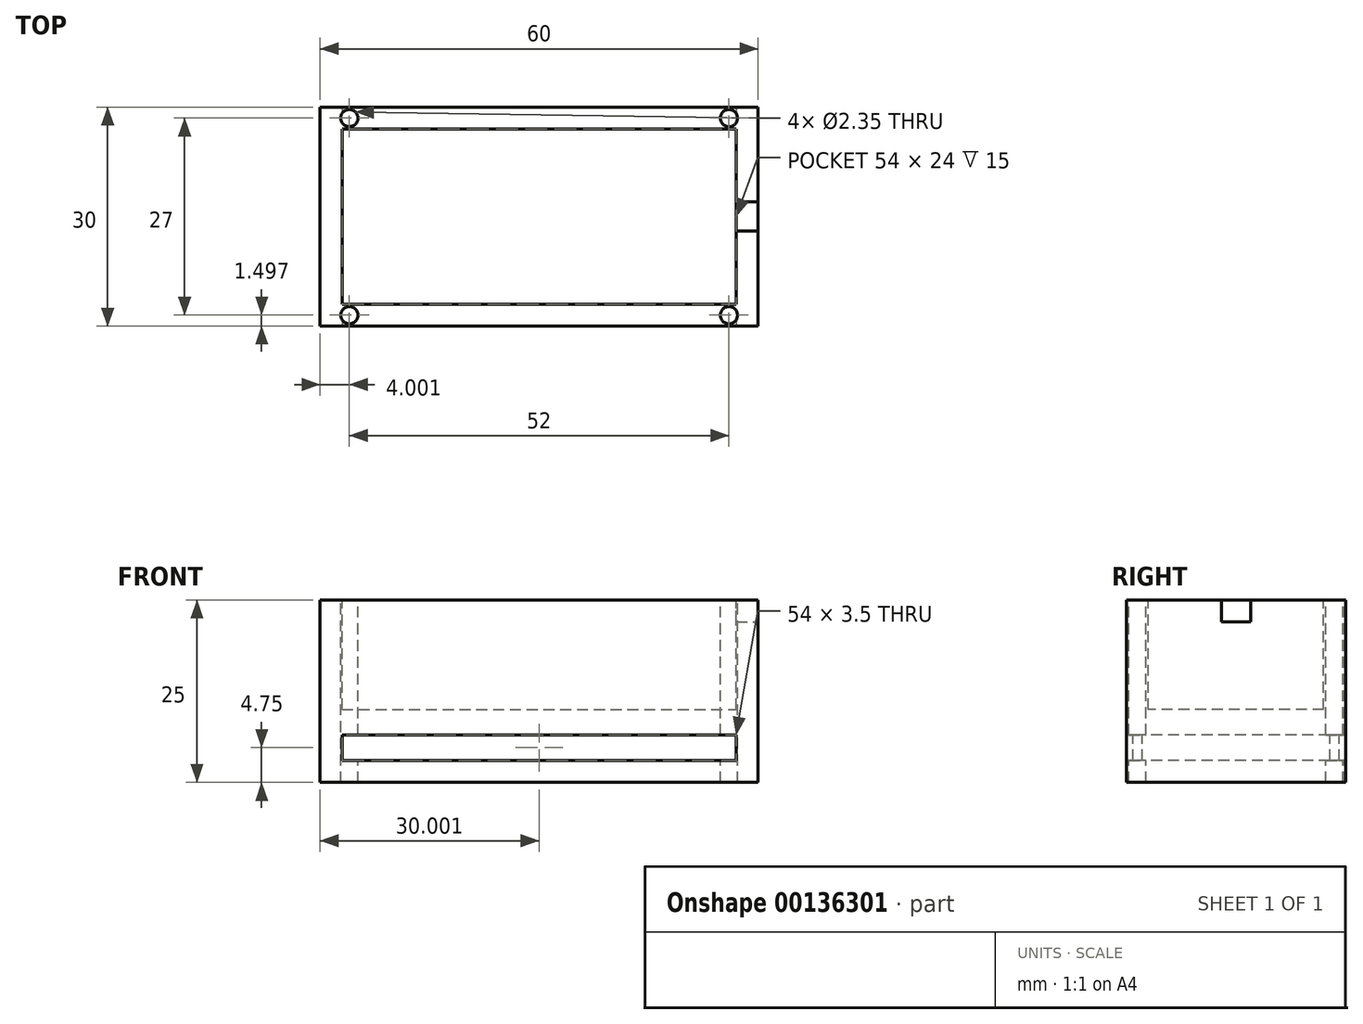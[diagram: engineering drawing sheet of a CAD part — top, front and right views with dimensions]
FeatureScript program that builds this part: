
annotation { "Feature Type Name" : "Feature", "Feature Type Description" : "" }
export const myFeature = defineFeature(function(context is Context, id is Id, definition is map)
    precondition{}
    {
        {
            var Q0;
            Q0=qCreatedBy(makeId("Top.planeOp"),FACE);
            var sketch = newSketch(context, id + "F0", { "sketchPlane" : qUnion([Q0])});
            skLineSegment(sketch, "E0.bottom", {"start": v(-30, 14.8) * mm, "end": v(30, 14.8) * mm});
            skLineSegment(sketch, "E0.top", {"start": v(-30, -15.2) * mm, "end": v(30, -15.2) * mm});
            skLineSegment(sketch, "E0.left", {"start": v(-30, 14.8) * mm, "end": v(-30, -15.2) * mm});
            skLineSegment(sketch, "E0.right", {"start": v(30, 14.8) * mm, "end": v(30, -15.2) * mm});
            skSolve(sketch);
        }
        {
            var Q0;
            Q0 = qSketchRegion(id + "F0", true);
            extrude(context, id + "F1", {"entities" : qUnion([Q0]), "depth" : 25 * mm});
        }
        {
            var Q0;
            Q0=makeQuery(id+"F1.opExtrude","SWEPT_FACE",FACE,{"disambiguationData":[OSD([sQuery(id+"F0.wireOp",EDGE,"E0.top")])]});
            var sketch = newSketch(context, id + "F2", { "sketchPlane" : qUnion([Q0])});
            skLineSegment(sketch, "E1.bottom", {"start": v(-27, 6.5) * mm, "end": v(27, 6.5) * mm});
            skLineSegment(sketch, "E1.top", {"start": v(-27, 3) * mm, "end": v(27, 3) * mm});
            skLineSegment(sketch, "E1.left", {"start": v(-27, 6.5) * mm, "end": v(-27, 3) * mm});
            skLineSegment(sketch, "E1.right", {"start": v(27, 6.5) * mm, "end": v(27, 3) * mm});
            skSolve(sketch);
        }
        {
            var Q0;
            Q0 = qSketchRegion(id + "F2", true);
            extrude(context, id + "F3", {"entities" : qUnion([Q0]), "operationType" : NewBodyOperationType.REMOVE, "endBound" : BoundingType.THROUGH_ALL, "oppositeDirection" : true, "depth" : 25 * mm});
        }
        {
            var Q0;
            Q0=makeQuery(id+"F1.opExtrude","CAP_FACE",FACE,{"disambiguationData":[OSD([sQuery(id+"F0.wireOp",EDGE,"E0.bottom"),sQuery(id+"F0.wireOp",EDGE,"E0.top"),sQuery(id+"F0.wireOp",EDGE,"E0.left"),sQuery(id+"F0.wireOp",EDGE,"E0.right")])],"isStart":false});
            var sketch = newSketch(context, id + "F4", { "sketchPlane" : qUnion([Q0])});
            skLineSegment(sketch, "E2.bottom", {"start": v(-27, 11.8) * mm, "end": v(27, 11.8) * mm});
            skLineSegment(sketch, "E2.top", {"start": v(-27, -12.2) * mm, "end": v(27, -12.2) * mm});
            skLineSegment(sketch, "E2.left", {"start": v(-27, 11.8) * mm, "end": v(-27, -12.2) * mm});
            skLineSegment(sketch, "E2.right", {"start": v(27, 11.8) * mm, "end": v(27, -12.2) * mm});
            skSolve(sketch);
        }
        {
            var Q0;
            Q0 = qSketchRegion(id + "F4", true);
            extrude(context, id + "F5", {"entities" : qUnion([Q0]), "operationType" : NewBodyOperationType.REMOVE, "oppositeDirection" : true, "depth" : 15 * mm});
        }
        {
            var Q0;
            Q0=makeQuery(id+"F1.opExtrude","CAP_FACE",FACE,{"disambiguationData":[OSD([sQuery(id+"F0.wireOp",EDGE,"E0.bottom"),sQuery(id+"F0.wireOp",EDGE,"E0.top"),sQuery(id+"F0.wireOp",EDGE,"E0.left"),sQuery(id+"F0.wireOp",EDGE,"E0.right")])],"isStart":false});
            var sketch = newSketch(context, id + "F6", { "sketchPlane" : qUnion([Q0])});
            skLineSegment(sketch, "E3.bottom", {"start": v(27, 1.8) * mm, "end": v(30, 1.8) * mm});
            skLineSegment(sketch, "E3.top", {"start": v(27, -2.2) * mm, "end": v(30, -2.2) * mm});
            skLineSegment(sketch, "E3.left", {"start": v(27, 1.8) * mm, "end": v(27, -2.2) * mm});
            skLineSegment(sketch, "E3.right", {"start": v(30, 1.8) * mm, "end": v(30, -2.2) * mm});
            skSolve(sketch);
        }
        {
            var Q0;
            Q0=makeQuery(id+"F6.imprint","IMPRINT",FACE,{"disambiguationData":[TD([[makeQuery(id+"F6.imprint","IMPRINT",EDGE,{"derivedFrom":sQuery(id+"F6.wireOp",EDGE,"E3.bottom")}),-1.0]])]});
            extrude(context, id + "F7", {"entities" : qUnion([Q0]), "operationType" : NewBodyOperationType.REMOVE, "oppositeDirection" : true, "depth" : 3 * mm});
        }
        {
            var Q0;
            Q0=makeQuery(id+"F1.opExtrude","CAP_FACE",FACE,{"disambiguationData":[OSD([sQuery(id+"F0.wireOp",EDGE,"E0.bottom"),sQuery(id+"F0.wireOp",EDGE,"E0.top"),sQuery(id+"F0.wireOp",EDGE,"E0.left"),sQuery(id+"F0.wireOp",EDGE,"E0.right")])],"isStart":false});
            var sketch = newSketch(context, id + "F8", { "sketchPlane" : qUnion([Q0])});
            skCircle(sketch, "E4", {"center": v(26, 13.29) * mm, "radius": 1.18 * mm});
            skCircle(sketch, "E5", {"center": v(-26, 13.3) * mm, "radius": 1.18 * mm});
            skCircle(sketch, "E6", {"center": v(-26, -13.7) * mm, "radius": 1.18 * mm});
            skCircle(sketch, "E7", {"center": v(26, -13.7) * mm, "radius": 1.18 * mm});
            skSolve(sketch);
        }
        {
            var Q0;
            Q0 = qSketchRegion(id + "F8", true);
            extrude(context, id + "F9", {"entities" : qUnion([Q0]), "operationType" : NewBodyOperationType.REMOVE, "endBound" : BoundingType.THROUGH_ALL, "oppositeDirection" : true, "depth" : 14 * mm});
        }
    });
